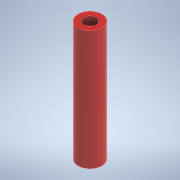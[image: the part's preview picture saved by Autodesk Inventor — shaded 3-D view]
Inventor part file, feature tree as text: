
AUTODESK INVENTOR PART (.ipt)
format: ipt  version: 2021 (Build 250183000, 183)  size: 101,888 bytes
history: native  units: mm
features: sketch x2, revolve x1, hole x1
ambient origin geometry x8: Origin, YZ Plane, XZ Plane, XY Plane, X Axis, Y Axis, Z Axis, Center Point
bodies: Solid1 (feature_tree)
feature tree (4):
  revolve  "Revolution1"  [1 undecoded]
  hole  "Hole1"  [1 undecoded]
  sketch  "Sketch1"  dims[d0=0.0mm d1=15.0mm]
  sketch  "Sketch2"  dims[d2=150.0mm d3=90.0deg d4=16.0mm d5=6.0mm d6=4.0mm d7=2.0mm d8=90.0deg d9=8.0mm d10=20.594885mm]
note: 2 required parameter values undecoded (feature->parameter linkage not recoverable at this tier; creation-order binding heuristic only, values carry confidence <= 0.55)